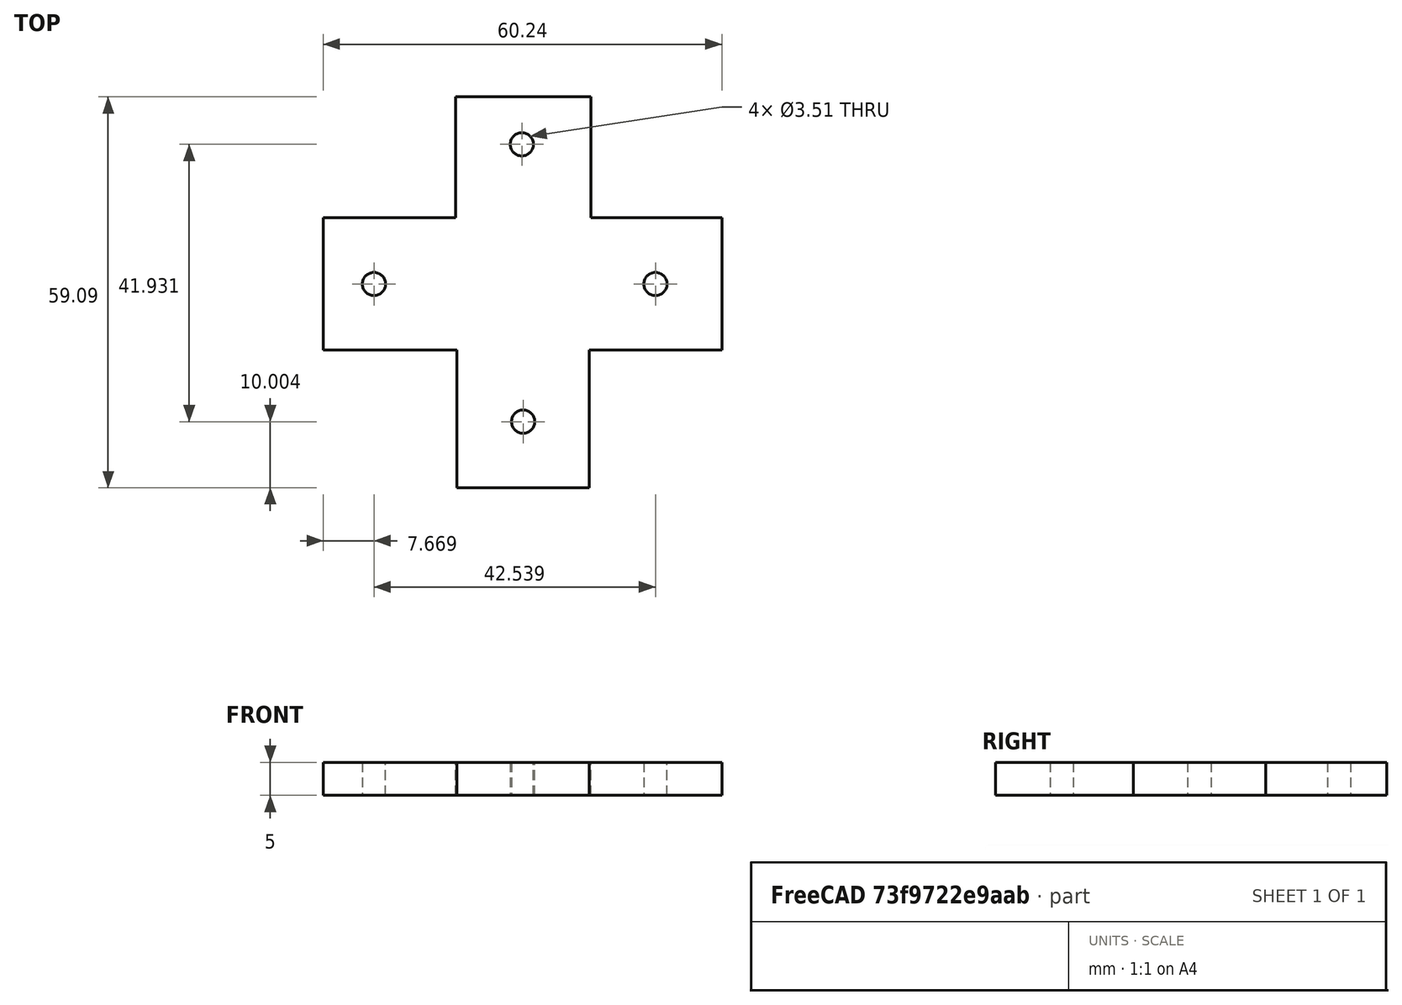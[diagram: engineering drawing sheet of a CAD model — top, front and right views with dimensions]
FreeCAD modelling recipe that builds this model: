
FCSTD DOCUMENT  (FreeCAD 0.21R33694 (Git))
Label: OJT1_T019_R02_cre_4forats
License: All rights reserved
LicenseURL: http://en.wikipedia.org/wiki/All_rights_reserved
objects: Sketcher::SketchObject×1, PartDesign::Pad×1, PartDesign::Body×1
note: 4 computed .brp shape members not serialized (recipe doc carries the construction recipe); baked Part::Feature solids carry a one-line shape summary decoded from their .brp

FEATURE [Sketcher::SketchObject] Sketch
  FullyConstrained = false
  MapMode = 5
  Support = -> [XY_Plane]
  sketch-geometry (16):
    g0: LineSegment StartX=-10.1085 StartY=30.0434 StartZ=0 EndX=10.3037 EndY=30.0434 EndZ=0
    g1: LineSegment StartX=10.3037 StartY=30.0434 StartZ=0 EndX=10.3037 EndY=11.7533 EndZ=0
    g2: LineSegment StartX=10.3037 StartY=11.7533 StartZ=0 EndX=30.1187 EndY=11.7533 EndZ=0
    g3: LineSegment StartX=30.1187 StartY=11.7533 StartZ=0 EndX=30.1187 EndY=-8.24674 EndZ=0
    g4: LineSegment StartX=30.1187 StartY=-8.24674 StartZ=0 EndX=10.0876 EndY=-8.24674 EndZ=0
    g5: LineSegment StartX=10.0876 StartY=-8.24674 StartZ=0 EndX=10.0876 EndY=-29.0464 EndZ=0
    g6: LineSegment StartX=10.0876 StartY=-29.0464 StartZ=0 EndX=-9.91235 EndY=-29.0464 EndZ=0
    g7: LineSegment StartX=-9.91235 StartY=-29.0464 StartZ=0 EndX=-9.91235 EndY=-8.24674 EndZ=0
    g8: LineSegment StartX=-9.91235 StartY=-8.24674 StartZ=0 EndX=-30.1187 EndY=-8.24674 EndZ=0
    g9: LineSegment StartX=-30.1187 StartY=-8.24674 StartZ=0 EndX=-30.1187 EndY=11.7533 EndZ=0
    g10: LineSegment StartX=-30.1187 StartY=11.7533 StartZ=0 EndX=-10.1085 EndY=11.7533 EndZ=0
    g11: LineSegment StartX=-10.1085 StartY=11.7533 StartZ=0 EndX=-10.1085 EndY=30.0434 EndZ=0
    g12: Circle CenterX=-0.108463 CenterY=22.885 CenterZ=0 NormalX=0 NormalY=0 NormalZ=1 AngleXU=0 Radius=1.75326
    g13: Circle CenterX=20.0876 CenterY=1.75326 CenterZ=0 NormalX=0 NormalY=0 NormalZ=1 AngleXU=0 Radius=1.75326
    g14: Circle CenterX=0.0876492 CenterY=-19.0464 CenterZ=0 NormalX=0 NormalY=0 NormalZ=1 AngleXU=0 Radius=1.75326
    g15: Circle CenterX=-22.4512 CenterY=1.75326 CenterZ=0 NormalX=0 NormalY=0 NormalZ=1 AngleXU=0 Radius=1.75326
  constraints (38):
    c: Horizontal(g0)
    c: Coincident(g1,g0)
    c: Vertical(g1)
    c: Coincident(g2,g1)
    c: Horizontal(g2)
    c: Coincident(g3,g2)
    c: Vertical(g3)
    c: Horizontal(g4)
    c: Coincident(g5,g4)
    c: Vertical(g5)
    c: Coincident(g6,g5)
    c: Horizontal(g6)
    c: Coincident(g7,g6)
    c: Vertical(g7)
    c: Coincident(g8,g7)
    c: Horizontal(g8)
    c: Coincident(g9,g8)
    c: Vertical(g9)
    c: Coincident(g10,g9)
    c: Horizontal(g10)
    c: Coincident(g11,g10)
    c: Coincident(g11,g0)
    c: Vertical(g11)
    c: Symmetric(g9,g2,g-2)
    c: Tangent(g15,g-1)
    c: Equal(g15,g12)
    c: Equal(g12,g13)
    c: Equal(g13,g14)
    c: DistanceX(g0,g12) = 10
    c: DistanceY(g13,g2) = 10
    c: DistanceY(g15,g9) = 10
    c: DistanceY(g5,g14) = 10
    c: DistanceX(g14,g4) = 10
    c: DistanceX(g7,g14) = 10
    c: DistanceX(g4,g13) = 10
    c: DistanceY(g3,g13) = 10
    c: Coincident(g4,g3)
    c: DistanceY(g8,g15) = 10
FEATURE [PartDesign::Pad] Pad
  Direction = (0,0,1)
  Length = 5
  Length2 = 10
  Profile = -> Sketch
  ReferenceAxis = -> Sketch [N_Axis]
  Type = 0
FEATURE [PartDesign::Body] Body
  Group = -> [Sketch,Pad]
  Origin = -> Origin
  Tip = -> Pad
